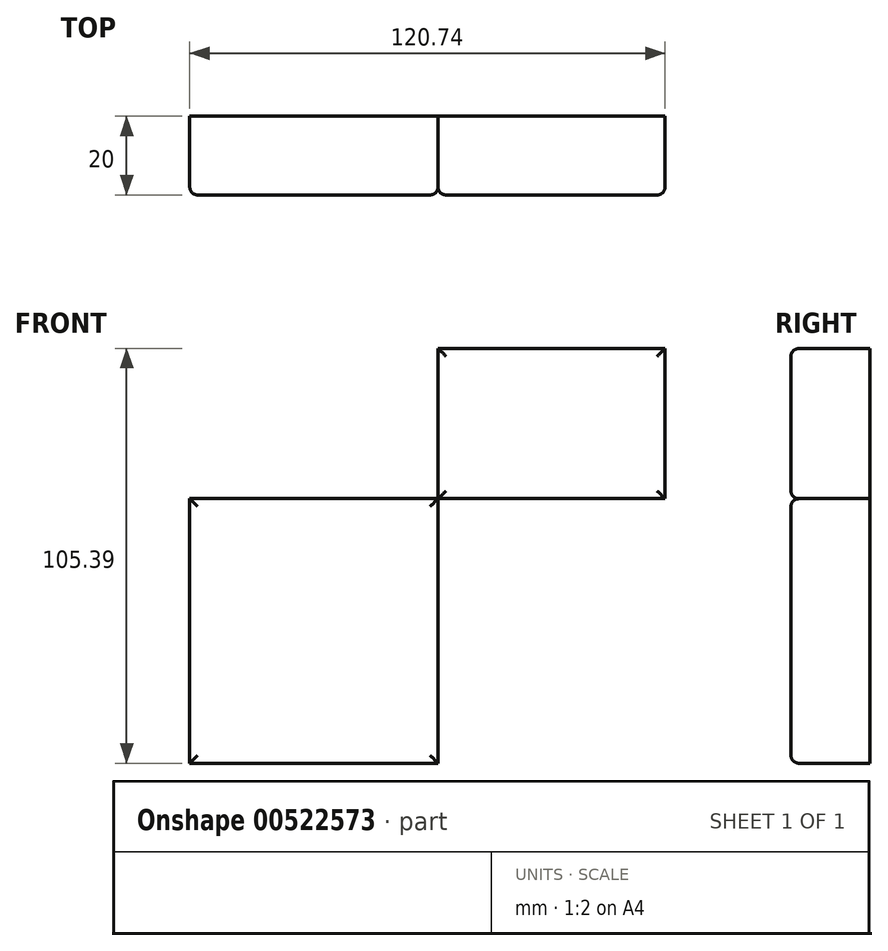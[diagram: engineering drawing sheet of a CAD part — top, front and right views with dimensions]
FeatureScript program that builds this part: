
annotation { "Feature Type Name" : "Feature", "Feature Type Description" : "" }
export const myFeature = defineFeature(function(context is Context, id is Id, definition is map)
    precondition{}
    {
        {
            var Q0;
            Q0=qCreatedBy(makeId("Front.planeOp"),FACE);
            var sketch = newSketch(context, id + "F0", { "sketchPlane" : qUnion([Q0])});
            skLineSegment(sketch, "E0.bottom", {"start": v(-53.32, -37.55) * mm, "end": v(9.75, -37.55) * mm});
            skLineSegment(sketch, "E0.top", {"start": v(-53.32, 29.67) * mm, "end": v(9.75, 29.67) * mm});
            skLineSegment(sketch, "E0.left", {"start": v(-53.32, -37.55) * mm, "end": v(-53.32, 29.67) * mm});
            skLineSegment(sketch, "E0.right", {"start": v(9.75, -37.55) * mm, "end": v(9.75, 29.67) * mm});
            skLineSegment(sketch, "E1.bottom", {"start": v(9.75, 29.67) * mm, "end": v(67.42, 29.67) * mm});
            skLineSegment(sketch, "E1.top", {"start": v(9.75, 67.84) * mm, "end": v(67.42, 67.84) * mm});
            skLineSegment(sketch, "E1.left", {"start": v(9.75, 29.67) * mm, "end": v(9.75, 67.84) * mm});
            skLineSegment(sketch, "E1.right", {"start": v(67.42, 29.67) * mm, "end": v(67.42, 67.84) * mm});
            skSolve(sketch);
        }
        {
            var Q0;
            Q0=makeQuery(id+"F0.imprint","IMPRINT",FACE,{"disambiguationData":[TD([[makeQuery(id+"F0.imprint","IMPRINT",EDGE,{"derivedFrom":sQuery(id+"F0.wireOp",EDGE,"E0.bottom")}),1.0]])]});
            var Q1;
            Q1=makeQuery(id+"F0.imprint","IMPRINT",FACE,{"disambiguationData":[TD([[makeQuery(id+"F0.imprint","IMPRINT",EDGE,{"derivedFrom":sQuery(id+"F0.wireOp",EDGE,"E1.bottom")}),1.0]])]});
            extrude(context, id + "F1", {"entities" : qUnion([Q0, Q1]), "depth" : 20 * mm, "offsetDistance" : 25.4 * mm});
        }
        {
            var Q0;
            Q0=makeQuery(id+"F1.opExtrude","CAP_EDGE",EDGE,{"disambiguationData":[OSD([sQuery(id+"F0.wireOp",EDGE,"E0.bottom")])],"isStart":false});
            var Q1;
            Q1=makeQuery(id+"F1.opExtrude","CAP_EDGE",EDGE,{"disambiguationData":[OSD([sQuery(id+"F0.wireOp",EDGE,"E0.left")])],"isStart":false});
            var Q2;
            Q2=makeQuery(id+"F1.opExtrude","CAP_EDGE",EDGE,{"disambiguationData":[OSD([sQuery(id+"F0.wireOp",EDGE,"E0.top")])],"isStart":false});
            var Q3;
            Q3=makeQuery(id+"F1.opExtrude","CAP_EDGE",EDGE,{"disambiguationData":[OSD([sQuery(id+"F0.wireOp",EDGE,"E0.right")])],"isStart":false});
            var Q4;
            Q4=makeQuery(id+"F1.opExtrude","CAP_EDGE",EDGE,{"disambiguationData":[OSD([sQuery(id+"F0.wireOp",EDGE,"E1.bottom")])],"isStart":false});
            var Q5;
            Q5=makeQuery(id+"F1.opExtrude","CAP_EDGE",EDGE,{"disambiguationData":[OSD([sQuery(id+"F0.wireOp",EDGE,"E1.top")])],"isStart":false});
            var Q6;
            Q6=makeQuery(id+"F1.opExtrude","CAP_EDGE",EDGE,{"disambiguationData":[OSD([sQuery(id+"F0.wireOp",EDGE,"E1.right")])],"isStart":false});
            var Q7;
            Q7=makeQuery(id+"F1.opExtrude","CAP_FACE",FACE,{"disambiguationData":[OSD([sQuery(id+"F0.wireOp",EDGE,"E1.bottom"),sQuery(id+"F0.wireOp",EDGE,"E1.top"),sQuery(id+"F0.wireOp",EDGE,"E1.left"),sQuery(id+"F0.wireOp",EDGE,"E1.right")])],"isStart":false});
            fillet(context, id + "F2", {"entities" : qUnion([Q0, Q1, Q2, Q3, Q4, Q5, Q6, Q7]), "radius" : 2 * mm, "tangentPropagation" : true, "allowEdgeOverflow" : false});
        }
    });
